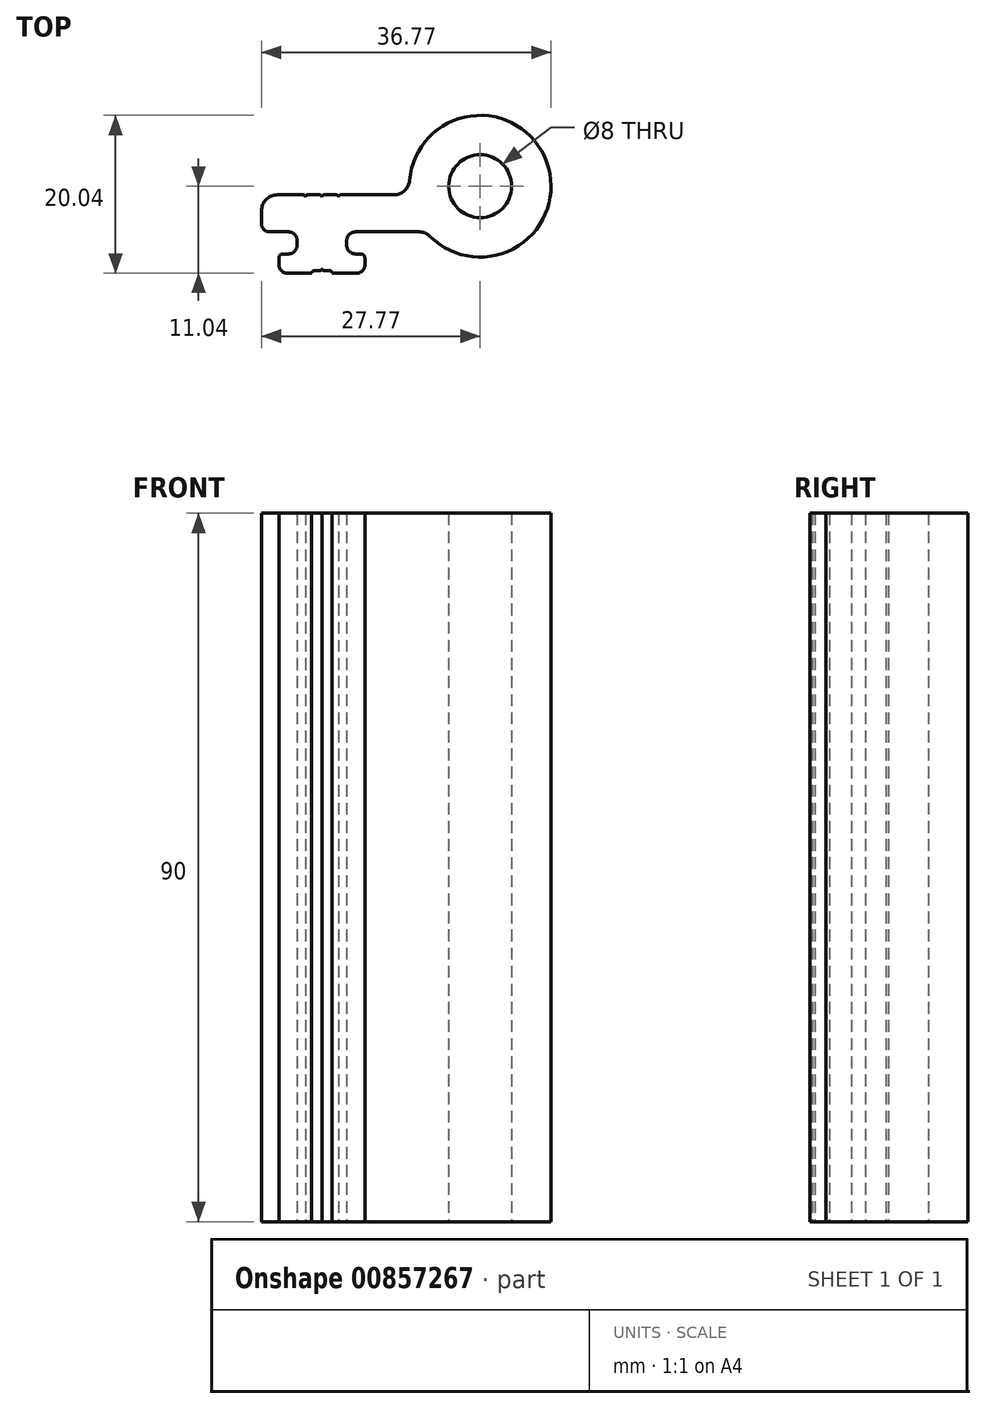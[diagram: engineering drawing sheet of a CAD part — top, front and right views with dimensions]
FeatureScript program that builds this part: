
annotation { "Feature Type Name" : "Feature", "Feature Type Description" : "" }
export const myFeature = defineFeature(function(context is Context, id is Id, definition is map)
    precondition{}
    {
        {
            var Q0;
            Q0=qCreatedBy(makeId("Top.planeOp"),FACE);
            var sketch = newSketch(context, id + "F0", { "sketchPlane" : qUnion([Q0])});
            skCircle(sketch, "E0", {"center": v(0, 0) * mm, "radius": 9 * mm});
            skCircle(sketch, "E1", {"center": v(0, 0) * mm, "radius": 4 * mm});
            skLineSegment(sketch, "E2", {"start": v(0, 0) * mm, "end": v(-45.8, 0) * mm, "construction": true});
            skLineSegment(sketch, "E3", {"start": v(-22.5, -1.1) * mm, "end": v(-25.77, -1.1) * mm});
            skLineSegment(sketch, "E4", {"start": v(-27.77, -3.1) * mm, "end": v(-27.77, -4.8) * mm});
            skLineSegment(sketch, "E5", {"start": v(-26.77, -5.8) * mm, "end": v(-24.35, -5.8) * mm});
            skPoint(sketch, "E6.visualSharp", {"position": v(-27.77, -1.1) * mm});
            skArc(sketch, "E6.filletArc", {"start": v(-25.77, -1.1) * mm, "mid": v(-27.18, -1.69) * mm, "end": v(-27.77, -3.1) * mm});
            skLineSegment(sketch, "E7", {"start": v(-23.25, -6.9) * mm, "end": v(-23.25, -7.5) * mm});
            skLineSegment(sketch, "E8", {"start": v(-24.35, -8.6) * mm, "end": v(-25.05, -8.6) * mm});
            skLineSegment(sketch, "E9", {"start": v(-25.55, -9.1) * mm, "end": v(-25.55, -10.04) * mm});
            skLineSegment(sketch, "E10", {"start": v(-24.55, -11.04) * mm, "end": v(-21.4, -11.04) * mm});
            skLineSegment(sketch, "E11", {"start": v(-14.65, -10.04) * mm, "end": v(-14.65, -9.1) * mm});
            skLineSegment(sketch, "E12", {"start": v(-15.15, -8.6) * mm, "end": v(-15.85, -8.6) * mm});
            skLineSegment(sketch, "E13", {"start": v(-16.95, -7.5) * mm, "end": v(-16.95, -6.9) * mm});
            skArc(sketch, "E14.filletArc", {"start": v(-15.65, -11.04) * mm, "mid": v(-14.94, -10.75) * mm, "end": v(-14.65, -10.04) * mm});
            skArc(sketch, "E15.filletArc", {"start": v(-25.55, -10.04) * mm, "mid": v(-25.26, -10.75) * mm, "end": v(-24.55, -11.04) * mm});
            skArc(sketch, "E16.filletArc", {"start": v(-22.2, -1.4) * mm, "mid": v(-22.29, -1.19) * mm, "end": v(-22.5, -1.1) * mm});
            skLineSegment(sketch, "E17", {"start": v(-21.72, -1.1) * mm, "end": v(-20.4, -1.1) * mm});
            skLineSegment(sketch, "E18", {"start": v(-17.7, -1.1) * mm, "end": v(-8.93, -1.1) * mm});
            skArc(sketch, "E19.filletArc", {"start": v(-18, -1.4) * mm, "mid": v(-18.09, -1.19) * mm, "end": v(-18.3, -1.1) * mm});
            skArc(sketch, "E20.filletArc", {"start": v(-17.7, -1.1) * mm, "mid": v(-17.91, -1.19) * mm, "end": v(-18, -1.4) * mm});
            skLineSegment(sketch, "E21", {"start": v(-19.8, -1.1) * mm, "end": v(-18.3, -1.1) * mm});
            skLineSegment(sketch, "E22", {"start": v(-21.4, -11.01) * mm, "end": v(-21.4, -11.04) * mm});
            skLineSegment(sketch, "E23", {"start": v(-19.8, -10.74) * mm, "end": v(-19.1, -10.74) * mm});
            skLineSegment(sketch, "E24", {"start": v(-18.8, -11.04) * mm, "end": v(-18.8, -11.04) * mm});
            skArc(sketch, "E25.filletArc", {"start": v(-21.1, -10.74) * mm, "mid": v(-21.31, -10.83) * mm, "end": v(-21.4, -11.04) * mm});
            skArc(sketch, "E26.filletArc", {"start": v(-18.8, -11.04) * mm, "mid": v(-18.89, -10.83) * mm, "end": v(-19.1, -10.74) * mm});
            skArc(sketch, "E27.filletArc", {"start": v(-20.1, -1.4) * mm, "mid": v(-20.19, -1.19) * mm, "end": v(-20.4, -1.1) * mm});
            skLineSegment(sketch, "E28.trimOffspring", {"start": v(-18.8, -11.04) * mm, "end": v(-15.65, -11.04) * mm});
            skArc(sketch, "E29.filletArc", {"start": v(-27.77, -4.8) * mm, "mid": v(-27.48, -5.5) * mm, "end": v(-26.77, -5.8) * mm});
            skArc(sketch, "E30.filletArc", {"start": v(-23.25, -6.9) * mm, "mid": v(-23.57, -6.12) * mm, "end": v(-24.35, -5.8) * mm});
            skArc(sketch, "E31.filletArc", {"start": v(-24.35, -8.6) * mm, "mid": v(-23.57, -8.28) * mm, "end": v(-23.25, -7.5) * mm});
            skArc(sketch, "E32.filletArc", {"start": v(-25.05, -8.6) * mm, "mid": v(-25.4, -8.75) * mm, "end": v(-25.55, -9.1) * mm});
            skLineSegment(sketch, "E33", {"start": v(-15.85, -5.8) * mm, "end": v(-6.88, -5.8) * mm});
            skArc(sketch, "E34.filletArc", {"start": v(-15.85, -5.8) * mm, "mid": v(-16.63, -6.12) * mm, "end": v(-16.95, -6.9) * mm});
            skArc(sketch, "E35.filletArc", {"start": v(-16.95, -7.5) * mm, "mid": v(-16.63, -8.28) * mm, "end": v(-15.85, -8.6) * mm});
            skArc(sketch, "E36.filletArc", {"start": v(-14.65, -9.1) * mm, "mid": v(-14.8, -8.75) * mm, "end": v(-15.15, -8.6) * mm});
            skArc(sketch, "E37.filletArc", {"start": v(-19.8, -1.1) * mm, "mid": v(-20.01, -1.19) * mm, "end": v(-20.1, -1.4) * mm});
            skLineSegment(sketch, "E38", {"start": v(-21.72, -1.1) * mm, "end": v(-21.9, -1.1) * mm});
            skArc(sketch, "E39.filletArc", {"start": v(-21.9, -1.1) * mm, "mid": v(-22.11, -1.19) * mm, "end": v(-22.2, -1.4) * mm});
            skLineSegment(sketch, "E40", {"start": v(9, 0) * mm, "end": v(9, -14.88) * mm, "construction": true});
            skLineSegment(sketch, "E41", {"start": v(-20.1, -0.66) * mm, "end": v(-20.1, -10.44) * mm, "construction": true});
            skLineSegment(sketch, "E42", {"start": v(-21.1, -10.74) * mm, "end": v(-20.4, -10.74) * mm});
            skArc(sketch, "E43.filletArc", {"start": v(-20.4, -10.74) * mm, "mid": v(-20.19, -10.66) * mm, "end": v(-20.1, -10.44) * mm});
            skArc(sketch, "E44.filletArc", {"start": v(-20.1, -10.44) * mm, "mid": v(-20.01, -10.66) * mm, "end": v(-19.8, -10.74) * mm});
            skSolve(sketch);
        }
        {
            var Q0;
            Q0 = qSketchRegion(id + "F0", true);
            extrude(context, id + "F1", {"entities" : qUnion([Q0]), "endBound" : BoundingType.SYMMETRIC, "depth" : 90 * mm, "offsetDistance" : 25 * mm});
        }
        {
            var Q0;
            Q0=makeQuery(id+"F1.opExtrude","SWEPT_EDGE",EDGE,{"disambiguationData":[OSD([sQuery(id+"F0.wireOp",EDGE,"E0"),sQuery(id+"F0.wireOp",EDGE,"E3")])]});
            fillet(context, id + "F2", {"entities" : qUnion([Q0]), "radius" : 2 * mm, "tangentPropagation" : true, "allowEdgeOverflow" : false});
        }
    });
